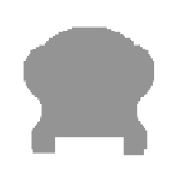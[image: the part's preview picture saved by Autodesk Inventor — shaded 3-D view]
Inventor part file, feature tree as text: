
AUTODESK INVENTOR PART (.ipt)
format: ipt  version: 2019 (Build 230136000, 136)  size: 129,536 bytes
history: native  units: mm
features: other x7, sketch x1, extrude x1
ambient origin geometry x8: Origin, YZ Plane, XZ Plane, XY Plane, X Axis, Y Axis, Z Axis, Center Point
bodies: Body1 (feature_tree)
feature tree (9):
  other  "Твердое тело1"
  other  "Блоки"
  sketch  "Эскиз"
  other  "Начальная плоскость"
  other  "РабПлоскость2"
  extrude  "Тело"  TaperAngle=0.0deg  [1 undecoded]
  other  "Конечная плоскость"
  other  "Поручень"
  other  "Поручень:1"
note: 1 required parameter value undecoded (feature->parameter linkage not recoverable at this tier; creation-order binding heuristic only, values carry confidence <= 0.55)
